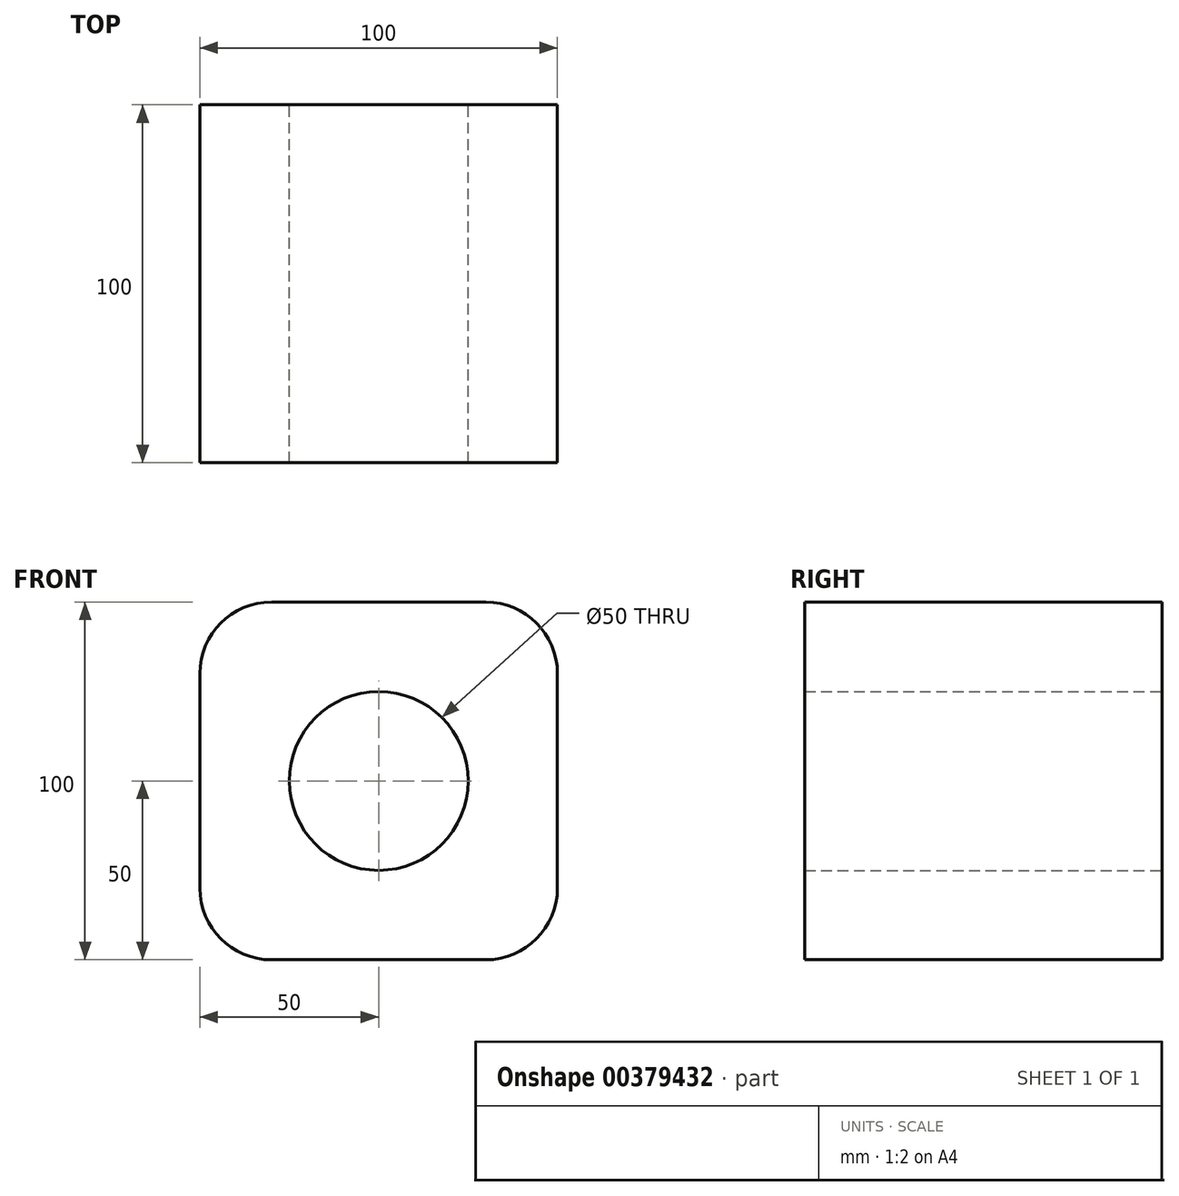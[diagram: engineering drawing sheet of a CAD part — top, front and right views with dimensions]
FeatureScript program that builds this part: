
annotation { "Feature Type Name" : "Feature", "Feature Type Description" : "" }
export const myFeature = defineFeature(function(context is Context, id is Id, definition is map)
    precondition{}
    {
        {
            var Q0;
            Q0=qCreatedBy(makeId("Front.planeOp"),FACE);
            var sketch = newSketch(context, id + "F0", { "sketchPlane" : qUnion([Q0])});
            skLineSegment(sketch, "E0.bottom", {"start": v(-30, -50) * mm, "end": v(30, -50) * mm});
            skLineSegment(sketch, "E0.top", {"start": v(-30, 50) * mm, "end": v(30, 50) * mm});
            skLineSegment(sketch, "E0.left", {"start": v(-50, -30) * mm, "end": v(-50, 30) * mm});
            skLineSegment(sketch, "E0.right", {"start": v(50, -30) * mm, "end": v(50, 30) * mm});
            skPoint(sketch, "E0.middle", {"position": v(0, 0) * mm});
            skPoint(sketch, "E1.visualSharp", {"position": v(-50, 50) * mm});
            skArc(sketch, "E1.filletArc", {"start": v(-30, 50) * mm, "mid": v(-44.14, 44.14) * mm, "end": v(-50, 30) * mm});
            skPoint(sketch, "E2.visualSharp", {"position": v(50, -50) * mm});
            skArc(sketch, "E2.filletArc", {"start": v(30, -50) * mm, "mid": v(44.14, -44.14) * mm, "end": v(50, -30) * mm});
            skPoint(sketch, "E3.visualSharp", {"position": v(50, 50) * mm});
            skArc(sketch, "E3.filletArc", {"start": v(50, 30) * mm, "mid": v(44.14, 44.14) * mm, "end": v(30, 50) * mm});
            skPoint(sketch, "E4.visualSharp", {"position": v(-50, -50) * mm});
            skArc(sketch, "E4.filletArc", {"start": v(-50, -30) * mm, "mid": v(-44.14, -44.14) * mm, "end": v(-30, -50) * mm});
            skCircle(sketch, "E5", {"center": v(0, 0) * mm, "radius": 25 * mm});
            skSolve(sketch);
        }
        {
            var Q0;
            Q0=makeQuery(id+"F0.imprint","IMPRINT",FACE,{"disambiguationData":[TD([[makeQuery(id+"F0.imprint","IMPRINT",EDGE,{"derivedFrom":sQuery(id+"F0.wireOp",EDGE,"E0.bottom")}),1.0]])]});
            extrude(context, id + "F1", {"entities" : qUnion([Q0]), "depth" : 100 * mm});
        }
    });
